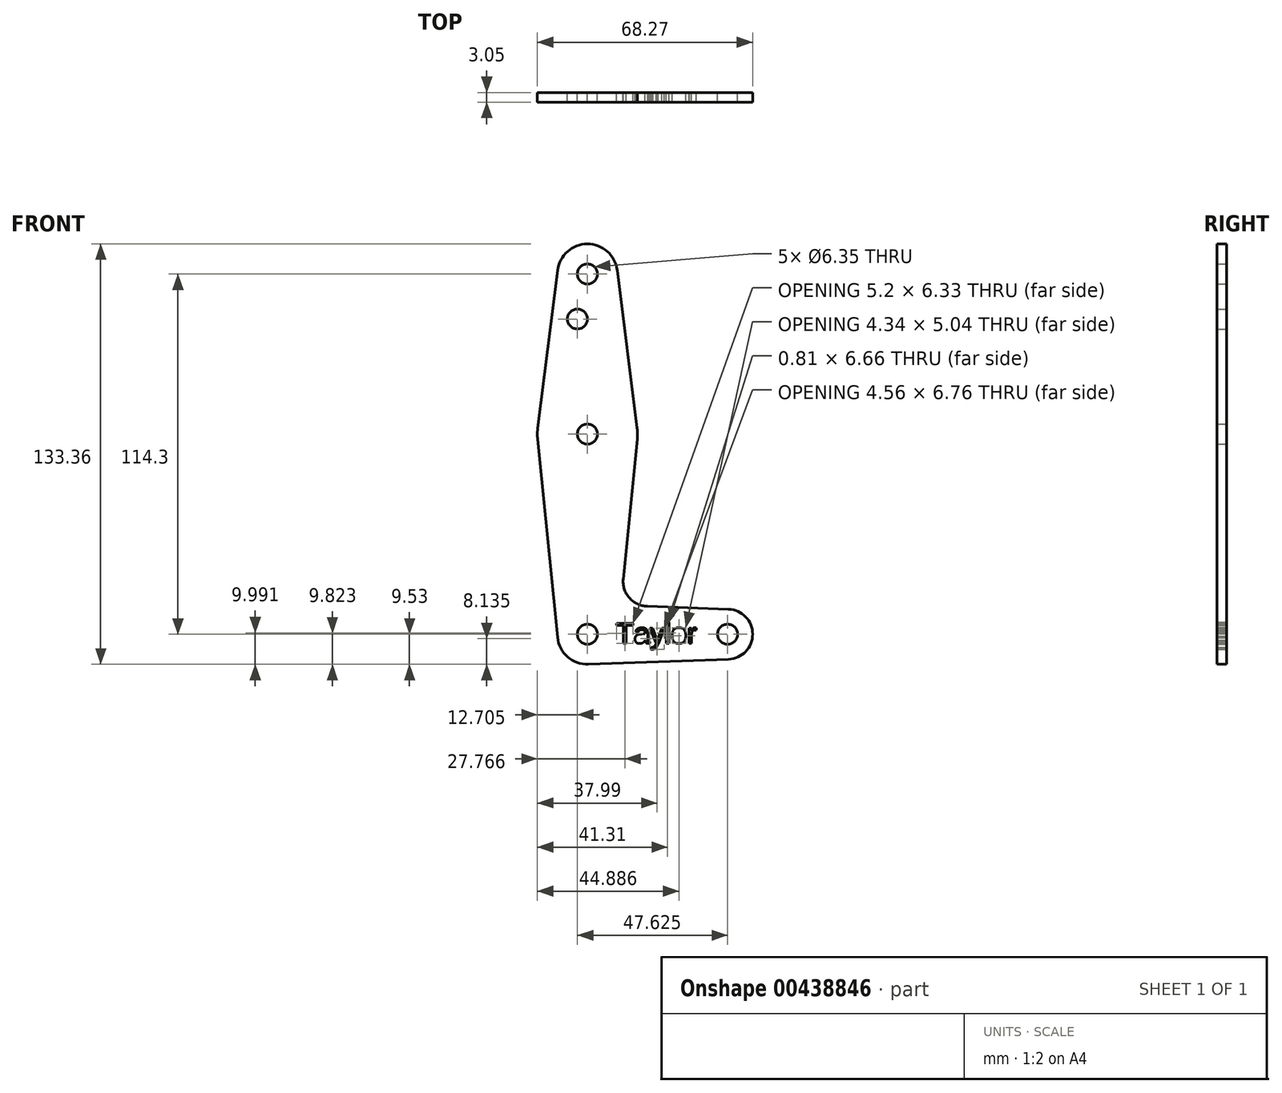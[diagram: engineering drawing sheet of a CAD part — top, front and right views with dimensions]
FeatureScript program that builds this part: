
annotation { "Feature Type Name" : "Feature", "Feature Type Description" : "" }
export const myFeature = defineFeature(function(context is Context, id is Id, definition is map)
    precondition{}
    {
        {
            var Q0;
            Q0=qCreatedBy(makeId("Front.planeOp"),FACE);
            var sketch = newSketch(context, id + "F0", { "sketchPlane" : qUnion([Q0])});
            skLineSegment(sketch, "E0", {"start": v(0, 0) * mm, "end": v(0, 114.3) * mm, "construction": true});
            skLineSegment(sketch, "E1", {"start": v(0, 0) * mm, "end": v(44.45, 0) * mm, "construction": true});
            skCircle(sketch, "E2", {"center": v(44.45, 0) * mm, "radius": 7.94 * mm});
            skCircle(sketch, "E3", {"center": v(0, 114.3) * mm, "radius": 9.53 * mm});
            skCircle(sketch, "E4", {"center": v(0, 0) * mm, "radius": 9.53 * mm});
            skCircle(sketch, "E5", {"center": v(0, 63.5) * mm, "radius": 15.88 * mm});
            skLineSegment(sketch, "E6", {"start": v(0, 0) * mm, "end": v(0, 63.5) * mm, "construction": true});
            skLineSegment(sketch, "E7", {"start": v(-15.75, 65.48) * mm, "end": v(-9.45, 115.5) * mm});
            skLineSegment(sketch, "E8", {"start": v(15.75, 65.48) * mm, "end": v(9.45, 115.5) * mm});
            skCircle(sketch, "E9", {"center": v(0, 114.3) * mm, "radius": 3.18 * mm});
            skCircle(sketch, "E10", {"center": v(0, 63.5) * mm, "radius": 3.18 * mm});
            skCircle(sketch, "E11", {"center": v(0, 0) * mm, "radius": 3.18 * mm});
            skCircle(sketch, "E12", {"center": v(44.45, 0) * mm, "radius": 3.18 * mm});
            skCircle(sketch, "E13", {"center": v(-3.18, 100.03) * mm, "radius": 3.18 * mm});
            skLineSegment(sketch, "E14", {"start": v(0, 63.5) * mm, "end": v(0, 100.03) * mm, "construction": true});
            skLineSegment(sketch, "E15", {"start": v(0, 100.03) * mm, "end": v(-3.18, 100.03) * mm, "construction": true});
            skLineSegment(sketch, "E16", {"start": v(11.34, 17.6) * mm, "end": v(15.8, 61.91) * mm});
            skLineSegment(sketch, "E17", {"start": v(-9.48, -0.95) * mm, "end": v(-15.8, 61.91) * mm});
            skLineSegment(sketch, "E18", {"start": v(18.97, 8.85) * mm, "end": v(44.73, 7.93) * mm});
            skLineSegment(sketch, "E19", {"start": v(0.34, -9.52) * mm, "end": v(44.73, -7.93) * mm});
            skArc(sketch, "E20.filletArc", {"start": v(11.34, 17.6) * mm, "mid": v(13.26, 11.57) * mm, "end": v(18.97, 8.85) * mm});
            skText(sketch, "E21", { "text": "Taylor", "fontName": "Arimo-Regular.ttf"});
            const initialGuessF0  = {"E21": [0.00908, -0.00287, 1, 0, 0.00662]};
            skSetInitialGuess(sketch, initialGuessF0);
            skSolve(sketch);
        }
        {
            var Q0;
            Q0 = qSketchRegion(id + "F0", true);
            extrude(context, id + "F1", {"entities" : qUnion([Q0]), "depth" : 3.05 * mm});
        }
    });
